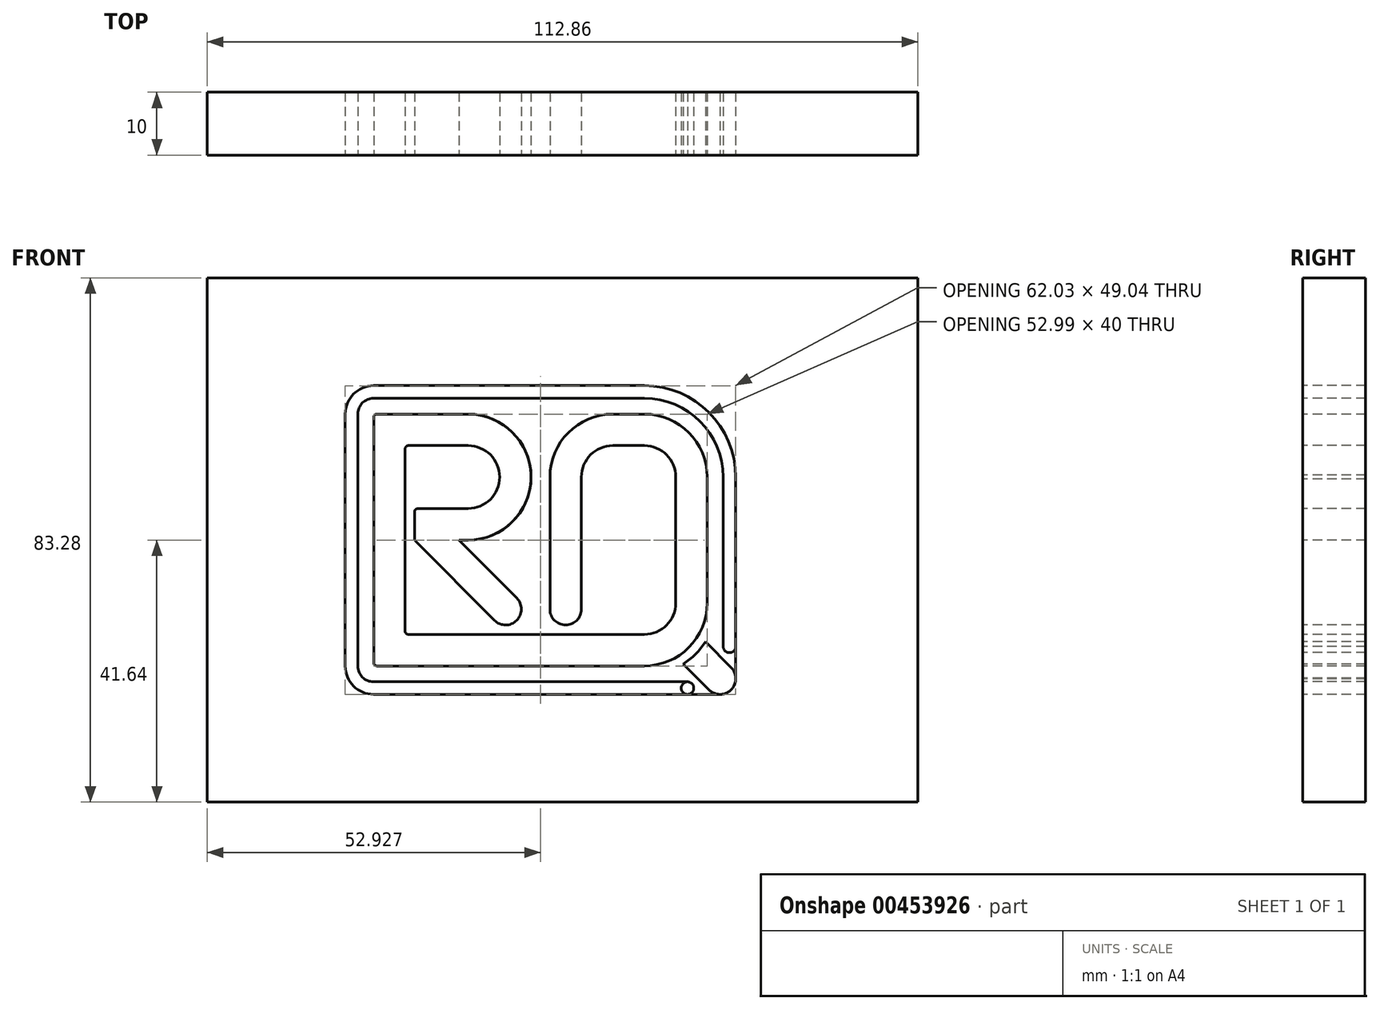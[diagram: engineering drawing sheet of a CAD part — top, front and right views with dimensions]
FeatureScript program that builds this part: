
annotation { "Feature Type Name" : "Feature", "Feature Type Description" : "" }
export const myFeature = defineFeature(function(context is Context, id is Id, definition is map)
    precondition{}
    {
        {
            var Q0;
            Q0=qCreatedBy(makeId("Front.planeOp"),FACE);
            var sketch = newSketch(context, id + "F0", { "sketchPlane" : qUnion([Q0])});
            skPoint(sketch, "E0.middle", {"position": v(0, 0) * mm});
            skLineSegment(sketch, "E1", {"start": v(-25, 14.5) * mm, "end": v(-25, -14.5) * mm});
            skLineSegment(sketch, "E2", {"start": v(-2, -20) * mm, "end": v(-0.38, -20) * mm});
            skLineSegment(sketch, "E3", {"start": v(-2, -11) * mm, "end": v(-2, 10) * mm});
            skLineSegment(sketch, "E4", {"start": v(8, 20) * mm, "end": v(13, 20) * mm});
            skLineSegment(sketch, "E5", {"start": v(23, 10) * mm, "end": v(23, -10) * mm});
            skLineSegment(sketch, "E6", {"start": v(13, -20) * mm, "end": v(9, -20) * mm});
            skLineSegment(sketch, "E7", {"start": v(-25, 20) * mm, "end": v(-15, 20) * mm});
            skLineSegment(sketch, "E8", {"start": v(-23.5, 0) * mm, "end": v(-15, 0) * mm});
            skLineSegment(sketch, "E9", {"start": v(-23.35, -0.15) * mm, "end": v(-10.82, -12.76) * mm});
            skLineSegment(sketch, "E10", {"start": v(-5, 10.33) * mm, "end": v(-5, 10.33) * mm});
            skPoint(sketch, "E11.visualSharp", {"position": v(-5.33, 20) * mm});
            skArc(sketch, "E11.filletArc", {"start": v(-5, 10.33) * mm, "mid": v(-8.05, 17.19) * mm, "end": v(-15, 20) * mm});
            skArc(sketch, "E12.filletArc", {"start": v(-15, 0) * mm, "mid": v(-7.81, 3.05) * mm, "end": v(-5, 10.33) * mm});
            skPoint(sketch, "E13.visualSharp", {"position": v(-3.63, -20) * mm});
            skPoint(sketch, "E14.visualSharp", {"position": v(23, -20) * mm});
            skArc(sketch, "E14.filletArc", {"start": v(13, -20) * mm, "mid": v(20.07, -17.07) * mm, "end": v(23, -10) * mm});
            skPoint(sketch, "E15.visualSharp", {"position": v(23, 20) * mm});
            skArc(sketch, "E15.filletArc", {"start": v(23, 10) * mm, "mid": v(20.07, 17.07) * mm, "end": v(13, 20) * mm});
            skPoint(sketch, "E16.visualSharp", {"position": v(-2, 20) * mm});
            skArc(sketch, "E16.filletArc", {"start": v(8, 20) * mm, "mid": v(0.92, 17.07) * mm, "end": v(-2, 10) * mm});
            skPoint(sketch, "E17.visualSharp", {"position": v(-2, -20) * mm});
            skArc(sketch, "E18.0", {"start": v(8, 15) * mm, "mid": v(4.46, 13.54) * mm, "end": v(3, 10) * mm});
            skLineSegment(sketch, "E18.1", {"start": v(3, -11) * mm, "end": v(3, 10) * mm});
            skLineSegment(sketch, "E18.2", {"start": v(8, 15) * mm, "end": v(13, 15) * mm});
            skArc(sketch, "E18.4", {"start": v(18, 10) * mm, "mid": v(16.53, 13.54) * mm, "end": v(13, 15) * mm});
            skLineSegment(sketch, "E18.5", {"start": v(18, 10) * mm, "end": v(18, -10) * mm});
            skArc(sketch, "E18.6", {"start": v(13, -15) * mm, "mid": v(16.53, -13.54) * mm, "end": v(18, -10) * mm});
            skLineSegment(sketch, "E18.7", {"start": v(13, -15) * mm, "end": v(9, -15) * mm});
            skLineSegment(sketch, "E19.0", {"start": v(-23, 5) * mm, "end": v(-15, 5) * mm});
            skArc(sketch, "E19.1", {"start": v(-15, 5) * mm, "mid": v(-11.44, 6.5) * mm, "end": v(-10, 10.08) * mm});
            skArc(sketch, "E19.2", {"start": v(-10, 10.08) * mm, "mid": v(-11.5, 13.56) * mm, "end": v(-15, 15) * mm});
            skLineSegment(sketch, "E19.3", {"start": v(-24.5, 15) * mm, "end": v(-15, 15) * mm});
            skLineSegment(sketch, "E20.0", {"start": v(-30, 17.5) * mm, "end": v(-30, -19.5) * mm});
            skLineSegment(sketch, "E21.0", {"start": v(-1, -15) * mm, "end": v(-0.38, -15) * mm});
            skLineSegment(sketch, "E21.2", {"start": v(-16.58, 0.12) * mm, "end": v(-7.27, -9.24) * mm});
            skLineSegment(sketch, "E22", {"start": v(-23.5, 4.5) * mm, "end": v(-23.5, 0.2) * mm});
            skLineSegment(sketch, "E23", {"start": v(-29.5, -20) * mm, "end": v(-25, -20) * mm});
            skLineSegment(sketch, "E24", {"start": v(-25, -20) * mm, "end": v(-2, -20) * mm});
            skLineSegment(sketch, "E25", {"start": v(-1, -15) * mm, "end": v(9, -15) * mm});
            skLineSegment(sketch, "E26.0", {"start": v(-24.5, -15) * mm, "end": v(0, -15) * mm});
            skLineSegment(sketch, "E27", {"start": v(-5, 10.33) * mm, "end": v(-5, 0) * mm});
            skLineSegment(sketch, "E28", {"start": v(0.5, -13.5) * mm, "end": v(0.5, -13.5) * mm});
            skPoint(sketch, "E29.visualSharp", {"position": v(3, -13.5) * mm});
            skArc(sketch, "E29.filletArc", {"start": v(0.5, -13.5) * mm, "mid": v(2.26, -12.77) * mm, "end": v(3, -11) * mm});
            skPoint(sketch, "E30.newPointB", {"position": v(-23.5, -13.5) * mm});
            skArc(sketch, "E30.filletArc", {"start": v(-2, -11) * mm, "mid": v(-1.27, -12.77) * mm, "end": v(0.5, -13.5) * mm});
            skPoint(sketch, "E31.visualSharp", {"position": v(-30, -20) * mm});
            skArc(sketch, "E31.filletArc", {"start": v(-30, -19.5) * mm, "mid": v(-29.85, -19.85) * mm, "end": v(-29.5, -20) * mm});
            skLineSegment(sketch, "E32", {"start": v(-7.28, -12.77) * mm, "end": v(-7.28, -12.77) * mm});
            skArc(sketch, "E33.filletArc", {"start": v(-7.28, -12.77) * mm, "mid": v(-6.55, -11) * mm, "end": v(-7.27, -9.24) * mm});
            skArc(sketch, "E34.filletArc", {"start": v(-10.82, -12.76) * mm, "mid": v(-9.05, -13.5) * mm, "end": v(-7.28, -12.77) * mm});
            skLineSegment(sketch, "E35.0", {"start": v(19.16, -19.7) * mm, "end": v(23.25, -23.79) * mm});
            skLineSegment(sketch, "E36.0", {"start": v(22.7, -16.17) * mm, "end": v(26.78, -20.25) * mm});
            skLineSegment(sketch, "E37.0", {"start": v(14.76, -15.3) * mm, "end": v(14.29, -14.83) * mm});
            skPoint(sketch, "E38.newPointB", {"position": v(-25, 20) * mm});
            skArc(sketch, "E38.filletArc", {"start": v(-24.5, 15) * mm, "mid": v(-24.85, 14.85) * mm, "end": v(-25, 14.5) * mm});
            skPoint(sketch, "E39.visualSharp", {"position": v(-23.5, 5) * mm});
            skArc(sketch, "E39.filletArc", {"start": v(-23, 5) * mm, "mid": v(-23.35, 4.85) * mm, "end": v(-23.5, 4.5) * mm});
            skPoint(sketch, "E40.visualSharp", {"position": v(-23.5, 0) * mm});
            skArc(sketch, "E40.filletArc", {"start": v(-23.5, 0.2) * mm, "mid": v(-23.46, 0.02) * mm, "end": v(-23.35, -0.15) * mm});
            skLineSegment(sketch, "E41", {"start": v(-30, 17.5) * mm, "end": v(-30, 19.5) * mm});
            skLineSegment(sketch, "E42", {"start": v(-25, 20) * mm, "end": v(-29.5, 20) * mm});
            skPoint(sketch, "E43.visualSharp", {"position": v(-30, 20) * mm});
            skArc(sketch, "E43.filletArc", {"start": v(-29.5, 20) * mm, "mid": v(-29.85, 19.85) * mm, "end": v(-30, 19.5) * mm});
            skArc(sketch, "E44", {"start": v(23.25, -23.79) * mm, "mid": v(26.78, -23.79) * mm, "end": v(26.78, -20.25) * mm});
            skPoint(sketch, "E45", {"position": v(20.07, -17.07) * mm});
            skPoint(sketch, "E46.orphan", {"position": v(16.53, -13.54) * mm});
            skLineSegment(sketch, "E47.trimOffspring", {"start": v(13, -20) * mm, "end": v(-0.38, -20) * mm});
            skArc(sketch, "E48.trimOffspring", {"start": v(19.16, -19.7) * mm, "mid": v(21.13, -18.13) * mm, "end": v(22.7, -16.17) * mm});
            skPoint(sketch, "E49.newPointB", {"position": v(-25, -20) * mm});
            skArc(sketch, "E49.filletArc", {"start": v(-25, -14.5) * mm, "mid": v(-24.85, -14.85) * mm, "end": v(-24.5, -15) * mm});
            skLineSegment(sketch, "E50", {"start": v(-15, 20) * mm, "end": v(8, 20) * mm});
            skLineSegment(sketch, "E51", {"start": v(21.86, -24.52) * mm, "end": v(-30.02, -24.52) * mm});
            skLineSegment(sketch, "E52", {"start": v(27.51, -22.08) * mm, "end": v(27.51, -18.86) * mm});
            skLineSegment(sketch, "E53", {"start": v(13, 24.52) * mm, "end": v(-30.02, 24.52) * mm});
            skLineSegment(sketch, "E54", {"start": v(-34.52, -20.02) * mm, "end": v(-34.52, 20.02) * mm});
            skPoint(sketch, "E55.orphan", {"position": v(17.43, -17.97) * mm});
            skPoint(sketch, "E56.orphan", {"position": v(13.35, -13.89) * mm});
            skArc(sketch, "E57.0", {"start": v(27.51, 10) * mm, "mid": v(23.26, 20.27) * mm, "end": v(13, 24.52) * mm});
            skArc(sketch, "E58.0", {"start": v(25.51, 10) * mm, "mid": v(21.85, 18.85) * mm, "end": v(13, 22.52) * mm});
            skLineSegment(sketch, "E59.0", {"start": v(25.51, -22.07) * mm, "end": v(25.51, -18.98) * mm});
            skLineSegment(sketch, "E60.0", {"start": v(25.02, -22.52) * mm, "end": v(21.98, -22.52) * mm});
            skLineSegment(sketch, "E61.0", {"start": v(-32.52, -20.02) * mm, "end": v(-32.52, 20.02) * mm});
            skLineSegment(sketch, "E62.0", {"start": v(13, 22.52) * mm, "end": v(-30.02, 22.52) * mm});
            skPoint(sketch, "E63.visualSharp", {"position": v(-32.52, 22.52) * mm});
            skArc(sketch, "E63.filletArc", {"start": v(-30.02, 22.52) * mm, "mid": v(-31.79, 21.79) * mm, "end": v(-32.52, 20.02) * mm});
            skArc(sketch, "E64.0", {"start": v(-30.02, 24.52) * mm, "mid": v(-33.2, 23.2) * mm, "end": v(-34.52, 20.02) * mm});
            skPoint(sketch, "E65.visualSharp", {"position": v(-32.52, -22.52) * mm});
            skArc(sketch, "E65.filletArc", {"start": v(-32.52, -20.02) * mm, "mid": v(-31.79, -21.79) * mm, "end": v(-30.02, -22.52) * mm});
            skArc(sketch, "E66.0", {"start": v(-34.52, -20.02) * mm, "mid": v(-33.2, -23.2) * mm, "end": v(-30.02, -24.52) * mm});
            skLineSegment(sketch, "E67", {"start": v(26.51, -16.32) * mm, "end": v(26.51, -17.9) * mm});
            skLineSegment(sketch, "E68.0", {"start": v(18.1, -20.77) * mm, "end": v(22.19, -24.85) * mm, "construction": true});
            skLineSegment(sketch, "E69.0", {"start": v(23.76, -15.1) * mm, "end": v(27.84, -19.2) * mm, "construction": true});
            skCircle(sketch, "E70", {"center": v(19.85, -23.52) * mm, "radius": 1 * mm});
            skCircle(sketch, "E71", {"center": v(26.51, -16.9) * mm, "radius": 1 * mm});
            skLineSegment(sketch, "E72.trimOffspring", {"start": v(25.51, -16.9) * mm, "end": v(25.51, 10) * mm});
            skLineSegment(sketch, "E73.trimOffspring", {"start": v(27.51, -16.9) * mm, "end": v(27.51, 33) * mm});
            skLineSegment(sketch, "E74.trimOffspring", {"start": v(19.86, -22.52) * mm, "end": v(-30.02, -22.52) * mm});
            skLineSegment(sketch, "E75", {"start": v(21.86, -24.52) * mm, "end": v(25.02, -24.52) * mm});
            skLineSegment(sketch, "E76", {"start": v(27.51, -16.9) * mm, "end": v(27.51, -22.08) * mm});
            skLineSegment(sketch, "E77.bottom", {"start": v(-56.43, 41.64) * mm, "end": v(56.43, 41.64) * mm});
            skLineSegment(sketch, "E77.top", {"start": v(-56.43, -41.64) * mm, "end": v(56.43, -41.64) * mm});
            skLineSegment(sketch, "E77.left", {"start": v(-56.43, 41.64) * mm, "end": v(-56.43, -41.64) * mm});
            skLineSegment(sketch, "E77.right", {"start": v(56.43, 41.64) * mm, "end": v(56.43, -41.64) * mm});
            skSolve(sketch);
        }
        {
            var Q0;
            Q0=makeQuery(id+"F0.imprint","IMPRINT",FACE,{"disambiguationData":[TD([[makeQuery(id+"F0.imprint","IMPRINT",EDGE,{"derivedFrom":sQuery(id+"F0.wireOp",EDGE,"E1")}),-1.0]])]});
            var Q1;
            {var subQ6=sQuery(id+"F0.wireOp",EDGE,"E9");Q1=makeQuery(id+"F0.imprint","IMPRINT",FACE,{"disambiguationData":[TD([[makeQuery(id+"F0.imprint","IMPRINT",EDGE,{"derivedFrom":subQ6}),1.0]])]});}
            var Q2;
            {var subQ0=sQuery(id+"F0.wireOp",EDGE,"E44");var subQ1=makeQuery(id+"F0.imprint","INTERSECT",VERTEX,{"derivedFrom":[sQuery(id+"F0.wireOp",EDGE,"E36.0"),subQ0]});Q2=makeQuery(id+"F0.imprint","IMPRINT",FACE,{"disambiguationData":[TD([[makeQuery(id+"F0.imprint","IMPRINT",EDGE,{"disambiguationData":[TD([[subQ1,-1.0]])],"derivedFrom":subQ0}),1.0]])]});}
            var Q3;
            {var subQ1=sQuery(id+"F0.wireOp",EDGE,"E36.0");Q3=makeQuery(id+"F0.imprint","IMPRINT",FACE,{"disambiguationData":[TD([[makeQuery(id+"F0.imprint","IMPRINT",EDGE,{"derivedFrom":subQ1}),-1.0]])]});}
            var Q4;
            {var subQ0=sQuery(id+"F0.wireOp",EDGE,"E0.bottom");Q4=makeQuery(id+"F0.imprint","IMPRINT",FACE,{"disambiguationData":[TD([[makeQuery(id+"F0.imprint","IMPRINT",EDGE,{"derivedFrom":subQ0}),-1.0]])]});}
            var Q5;
            {var subQ0=sQuery(id+"F0.wireOp",EDGE,"E0.bottom");Q5=makeQuery(id+"F0.imprint","IMPRINT",FACE,{"disambiguationData":[TD([[makeQuery(id+"F0.imprint","IMPRINT",EDGE,{"derivedFrom":subQ0}),1.0]])]});}
            extrude(context, id + "F1", {"entities" : qUnion([Q0, Q1, Q2, Q3, Q4, Q5]), "oppositeDirection" : true, "depth" : 10 * mm});
        }
        {
            var Q0;
            Q0=makeQuery(id+"F0.imprint","IMPRINT",FACE,{"disambiguationData":[TD([[makeQuery(id+"F0.imprint","IMPRINT",EDGE,{"derivedFrom":sQuery(id+"F0.wireOp",EDGE,"E1")}),1.0]])]});
            var Q1;
            {var subQ16=sQuery(id+"F0.wireOp",EDGE,"E2");Q1=makeQuery(id+"F0.imprint","IMPRINT",FACE,{"disambiguationData":[TD([[makeQuery(id+"F0.imprint","IMPRINT",EDGE,{"derivedFrom":subQ16}),-1.0]])]});}
            extrude(context, id + "F2", {"entities" : qUnion([Q0, Q1]), "oppositeDirection" : true, "depth" : 10 * mm});
        }
        {
            var Q0;
            Q0=makeQuery(id+"F0.imprint","IMPRINT",FACE,{"disambiguationData":[TD([[makeQuery(id+"F0.imprint","IMPRINT",EDGE,{"derivedFrom":sQuery(id+"F0.wireOp",EDGE,"E53")}),1.0]])]});
            var Q1;
            {var subQ0=sQuery(id+"F0.wireOp",EDGE,"E70");var subQ2=makeQuery(id+"F0.imprint","IMPRINT",VERTEX,{"derivedFrom":subQ0});Q1=makeQuery(id+"F0.imprint","IMPRINT",FACE,{"disambiguationData":[TD([[makeQuery(id+"F0.imprint","IMPRINT",EDGE,{"disambiguationData":[TD([[subQ2,-1.0]])],"derivedFrom":subQ0}),1.0]])]});}
            var Q2;
            {var subQ0=sQuery(id+"F0.wireOp",EDGE,"E71");var subQ3=makeQuery(id+"F0.imprint","IMPRINT",VERTEX,{"derivedFrom":subQ0});Q2=makeQuery(id+"F0.imprint","IMPRINT",FACE,{"disambiguationData":[TD([[makeQuery(id+"F0.imprint","IMPRINT",EDGE,{"disambiguationData":[TD([[subQ3,1.0]])],"derivedFrom":subQ0}),1.0]])]});}
            extrude(context, id + "F3", {"entities" : qUnion([Q0, Q1, Q2]), "oppositeDirection" : true, "depth" : 10 * mm});
        }
        {
            var Q0;
            Q0=makeQuery(id+"F0.imprint","IMPRINT",FACE,{"disambiguationData":[TD([[makeQuery(id+"F0.imprint","IMPRINT",EDGE,{"derivedFrom":sQuery(id+"F0.wireOp",EDGE,"E53")}),-1.0]])]});
            extrude(context, id + "F4", {"entities" : qUnion([Q0]), "oppositeDirection" : true, "depth" : 10 * mm});
        }
    });
